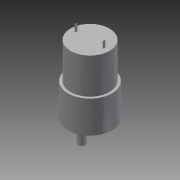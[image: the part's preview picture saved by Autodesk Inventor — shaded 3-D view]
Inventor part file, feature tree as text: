
AUTODESK INVENTOR PART (.ipt)
format: ipt  version: 2015 (Build 190159000, 159)  size: 203,776 bytes
history: native  units: mm
features: sketch x14, extrude x12, revolve x2, other x1
ambient origin geometry x8: Origin, YZ Plane, XZ Plane, XY Plane, X Axis, Y Axis, Z Axis, Center Point
bodies: Body1 (feature_tree)
feature tree (29):
  other  "Sólido1"
  extrude  "Extrusión1"  Depth=27.0mm TaperAngle=0.0deg
  extrude  "Extrusión2"  Depth=30.0mm TaperAngle=0.0deg
  extrude  "Extrusión3"  Depth=12.05mm
  sketch  "Boceto4"  dims[d9=5.6mm d10=0.0mm d19=7.0mm]
  extrude  "Extrusión4"  Depth=7.0mm
  extrude  "Extrusión5"  Depth=6.0mm TaperAngle=0.0deg
  extrude  "Extrusión6"  Depth=0.5mm TaperAngle=0.0deg
  revolve  "Revolución1"  Angle=90.0deg
  revolve  "Revolución2"  [1 undecoded]
  extrude  "Extrusión7"  Depth=1.0mm TaperAngle=0.0deg
  extrude  "Extrusión8"  Depth=10.0mm TaperAngle=0.0deg
  extrude  "Extrusión9"  [1 undecoded]
  extrude  "Extrusión10"  [1 undecoded]
  extrude  "Extrusión11"  [1 undecoded]
  extrude  "Extrusión12"  [1 undecoded]
  sketch  "Boceto14"
  sketch  "Boceto15"
  sketch  "Boceto1"  dims[d0=36.8mm d1=27.0mm d2=0.0mm]
  sketch  "Boceto2"  dims[d4=2.0mm d5=30.0mm d6=0.0mm]
  sketch  "Boceto3"  dims[d7=12.05mm d8=12.05mm]
  sketch  "Boceto5"  dims[d20=12.0mm d21=6.0mm d22=0.0mm]
  sketch  "Boceto6"  dims[d23=0.5mm d24=0.0mm d25=0.5mm d26=0.0mm]
  sketch  "Boceto7"  dims[d27=90.0deg d28=90.0deg]
  sketch  "Boceto8"  dims[d29=15.5mm d30=0.0mm d32=12.0mm d33=0.0mm]
  sketch  "Boceto9"  dims[d34=1.0mm d35=1.0mm d36=0.0mm]
  sketch  "Boceto10"  dims[d37=10.0mm d38=0.0mm d39=0.45mm d40=0.0mm]
  sketch  "Boceto12"  dims[d41=0.45mm d42=0.0mm]
  sketch  "Boceto13"
note: 5 required parameter values undecoded (feature->parameter linkage not recoverable at this tier; creation-order binding heuristic only, values carry confidence <= 0.55)